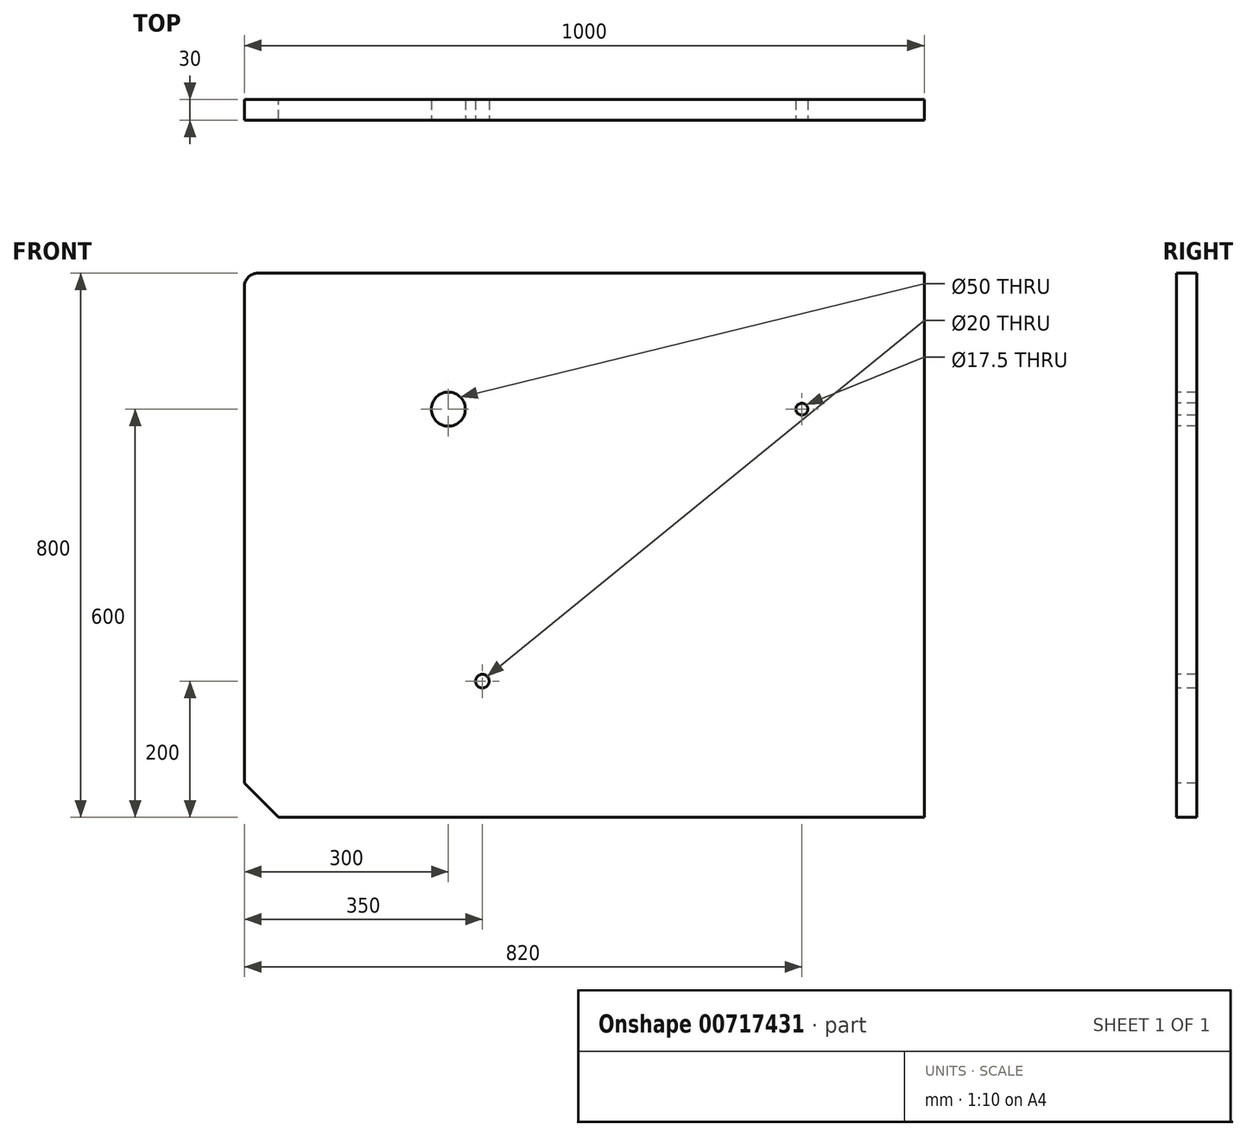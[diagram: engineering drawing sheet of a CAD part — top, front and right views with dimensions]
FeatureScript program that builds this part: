
annotation { "Feature Type Name" : "Feature", "Feature Type Description" : "" }
export const myFeature = defineFeature(function(context is Context, id is Id, definition is map)
    precondition{}
    {
        {
            var Q0;
            Q0=qCreatedBy(makeId("Front.planeOp"),FACE);
            var sketch = newSketch(context, id + "F0", { "sketchPlane" : qUnion([Q0])});
            skLineSegment(sketch, "E0.bottom", {"start": v(500, 400) * mm, "end": v(-500, 400) * mm});
            skLineSegment(sketch, "E0.top", {"start": v(500, -400) * mm, "end": v(-500, -400) * mm});
            skLineSegment(sketch, "E0.left", {"start": v(500, 400) * mm, "end": v(500, -400) * mm});
            skLineSegment(sketch, "E0.right", {"start": v(-500, 400) * mm, "end": v(-500, -400) * mm});
            skPoint(sketch, "E0.middle", {"position": v(0, 0) * mm});
            skSolve(sketch);
        }
        {
            var Q0;
            Q0=makeQuery(id+"F0.imprint","IMPRINT",FACE,{"disambiguationData":[TD([[makeQuery(id+"F0.imprint","IMPRINT",EDGE,{"derivedFrom":sQuery(id+"F0.wireOp",EDGE,"E0.bottom")}),1.0]])]});
            extrude(context, id + "F1", {"entities" : qUnion([Q0]), "endBound" : BoundingType.SYMMETRIC, "depth" : 30 * mm, "offsetDistance" : 25 * mm});
        }
        {
            var Q0;
            Q0=makeQuery(id+"F1.opExtrude","CAP_FACE",FACE,{"disambiguationData":[OSD([sQuery(id+"F0.wireOp",EDGE,"E0.bottom"),sQuery(id+"F0.wireOp",EDGE,"E0.top"),sQuery(id+"F0.wireOp",EDGE,"E0.left"),sQuery(id+"F0.wireOp",EDGE,"E0.right")])],"isStart":false});
            var sketch = newSketch(context, id + "F2", { "sketchPlane" : qUnion([Q0])});
            skPoint(sketch, "E1", {"position": v(-200, 200) * mm});
            skPoint(sketch, "E2", {"position": v(-150, -200) * mm});
            skPoint(sketch, "E3", {"position": v(320, 200) * mm});
            skSolve(sketch);
        }
        {
            var Q0;
            Q0=sQuery(id+"F2.wireOp",VERTEX,"E1");
            var Q1;
            Q1=makeQuery(id+"F1.opExtrude","SWEPT_BODY",BODY,{"disambiguationData":[OSD([sQuery(id+"F0.wireOp",EDGE,"E0.bottom"),sQuery(id+"F0.wireOp",EDGE,"E0.top"),sQuery(id+"F0.wireOp",EDGE,"E0.left"),sQuery(id+"F0.wireOp",EDGE,"E0.right")])]});
            hole(context, id + "F3", {"style" : HoleStyle.SIMPLE, "endStyle" : HoleEndStyle.THROUGH, "holeDiameter" : 50 * mm, "majorDiameter" : 5 * mm, "isTappedThrough" : true, "tappedDepth" : 12 * mm, "tapClearance" : 3, "locations" : qUnion([Q0]), "scope" : qUnion([Q1])});
        }
        {
            var Q0;
            Q0=sQuery(id+"F2.wireOp",VERTEX,"E2");
            var Q1;
            Q1=makeQuery(id+"F1.opExtrude","SWEPT_BODY",BODY,{"disambiguationData":[OSD([sQuery(id+"F0.wireOp",EDGE,"E0.bottom"),sQuery(id+"F0.wireOp",EDGE,"E0.top"),sQuery(id+"F0.wireOp",EDGE,"E0.left"),sQuery(id+"F0.wireOp",EDGE,"E0.right")])]});
            hole(context, id + "F4", {"style" : HoleStyle.SIMPLE, "endStyle" : HoleEndStyle.THROUGH, "holeDiameter" : 20 * mm, "majorDiameter" : 5 * mm, "isTappedThrough" : true, "tappedDepth" : 12 * mm, "tapClearance" : 3, "locations" : qUnion([Q0]), "scope" : qUnion([Q1])});
        }
        {
            var Q0;
            Q0=sQuery(id+"F2.wireOp",VERTEX,"E3");
            var Q1;
            Q1=makeQuery(id+"F1.opExtrude","SWEPT_BODY",BODY,{"disambiguationData":[OSD([sQuery(id+"F0.wireOp",EDGE,"E0.bottom"),sQuery(id+"F0.wireOp",EDGE,"E0.top"),sQuery(id+"F0.wireOp",EDGE,"E0.left"),sQuery(id+"F0.wireOp",EDGE,"E0.right")])]});
            hole(context, id + "F5", {"style" : HoleStyle.SIMPLE, "endStyle" : HoleEndStyle.THROUGH, "standardTappedOrClearance" : lookupTablePath({ "standard" : "ISO", "engagement" : "75%", "pitch" : "2.5 mm", "size" : "M20", "type" : "Tapped" }), "standardBlindInLast" : lookupTablePath({ "standard" : "ISO", "engagement" : "75%", "pitch" : "2.5 mm", "size" : "M20", "type" : "Tapped" }), "holeDiameter" : 17.5 * mm, "majorDiameter" : 20 * mm, "showTappedDepth" : true, "isTappedThrough" : true, "tappedDepth" : 12 * mm, "tapClearance" : 3, "locations" : qUnion([Q0]), "scope" : qUnion([Q1])});
        }
        {
            var Q0;
            Q0=makeQuery(id+"F1.opExtrude","SWEPT_EDGE",EDGE,{"disambiguationData":[OSD([sQuery(id+"F0.wireOp",EDGE,"E0.bottom"),sQuery(id+"F0.wireOp",EDGE,"E0.right")])]});
            fillet(context, id + "F6", {"entities" : qUnion([Q0]), "radius" : 20 * mm, "tangentPropagation" : true, "allowEdgeOverflow" : false});
        }
        {
            var Q0;
            Q0=makeQuery(id+"F1.opExtrude","SWEPT_EDGE",EDGE,{"disambiguationData":[OSD([sQuery(id+"F0.wireOp",EDGE,"E0.top"),sQuery(id+"F0.wireOp",EDGE,"E0.right")])]});
            chamfer(context, id + "F7", {"entities" : qUnion([Q0]), "width" : 50 * mm, "tangentPropagation" : true});
        }
    });
